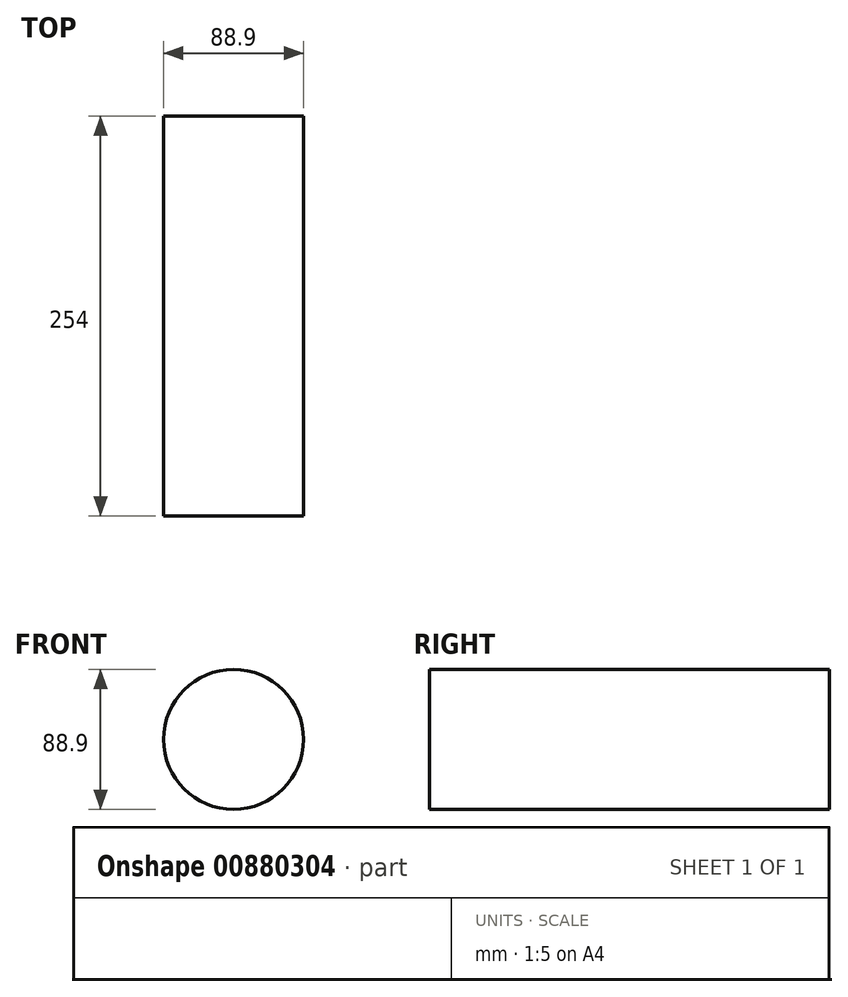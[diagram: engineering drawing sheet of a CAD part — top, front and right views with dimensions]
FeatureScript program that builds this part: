
annotation { "Feature Type Name" : "Feature", "Feature Type Description" : "" }
export const myFeature = defineFeature(function(context is Context, id is Id, definition is map)
    precondition{}
    {
        {
            var Q0;
            Q0=qCreatedBy(makeId("Front.planeOp"),FACE);
            var sketch = newSketch(context, id + "F0", { "sketchPlane" : qUnion([Q0])});
            skCircle(sketch, "E0", {"center": v(0, 0) * mm, "radius": 44.45 * mm});
            skSolve(sketch);
        }
        {
            var Q0;
            Q0=makeQuery(id+"F0.imprint","IMPRINT",FACE,{"disambiguationData":[TD([[makeQuery(id+"F0.imprint","IMPRINT",EDGE,{"derivedFrom":sQuery(id+"F0.wireOp",EDGE,"E0")}),1.0]])]});
            extrude(context, id + "F1", {"entities" : qUnion([Q0]), "endBound" : BoundingType.SYMMETRIC, "depth" : 254 * mm, "offsetDistance" : 25.4 * mm});
        }
    });
